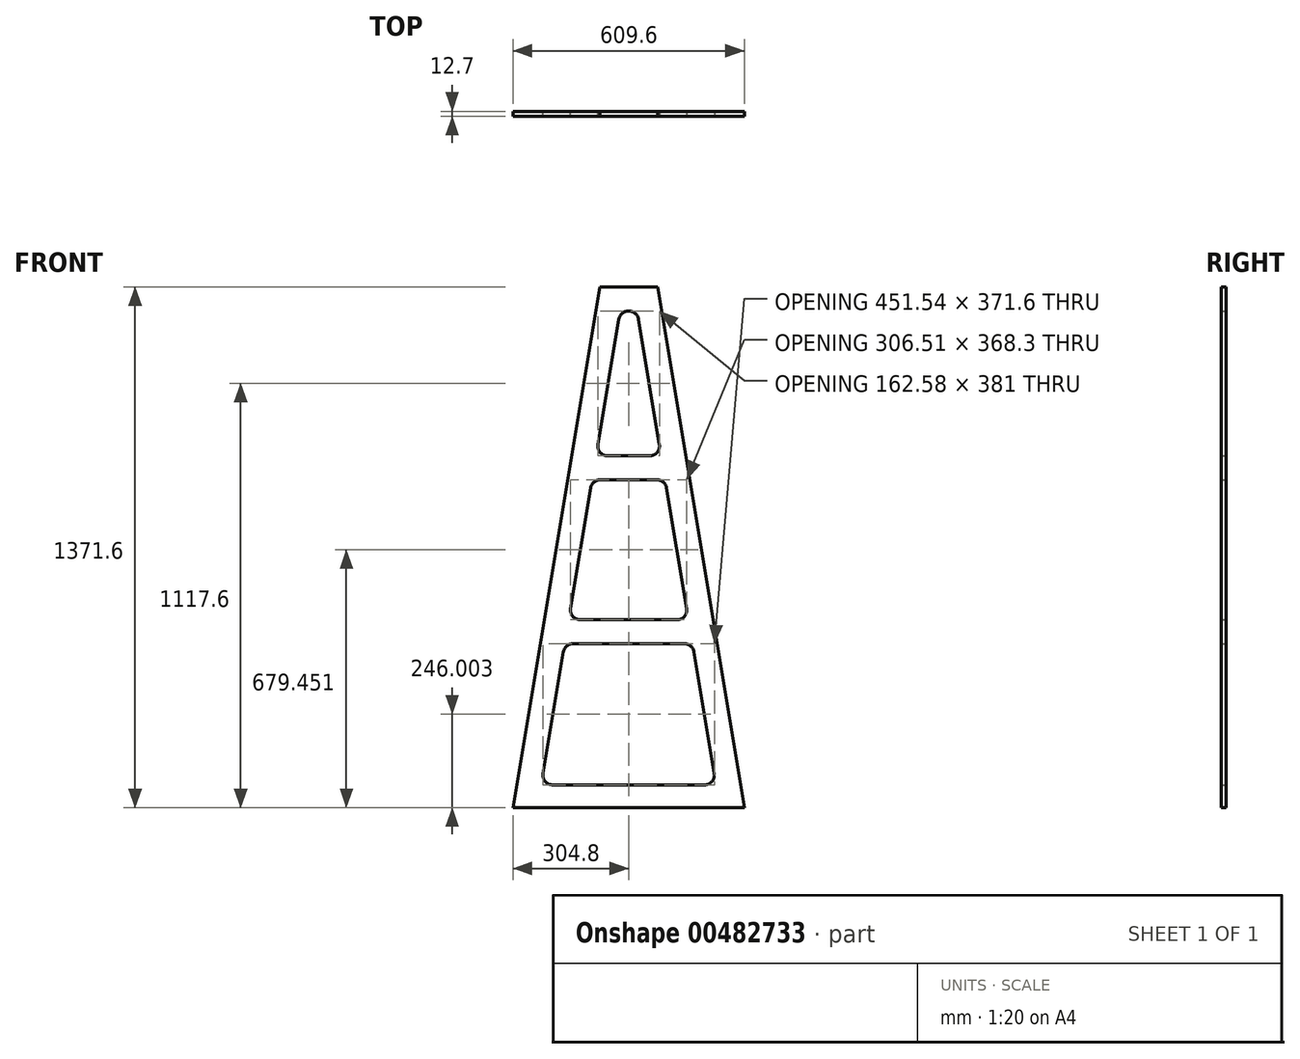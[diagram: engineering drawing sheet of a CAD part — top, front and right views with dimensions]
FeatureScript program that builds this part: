
annotation { "Feature Type Name" : "Feature", "Feature Type Description" : "" }
export const myFeature = defineFeature(function(context is Context, id is Id, definition is map)
    precondition{}
    {
        {
            var Q0;
            Q0=qCreatedBy(makeId("Front.planeOp"),FACE);
            var sketch = newSketch(context, id + "F0", { "sketchPlane" : qUnion([Q0])});
            skLineSegment(sketch, "E0", {"start": v(0, 220.15) * mm, "end": v(76.2, 220.15) * mm});
            skLineSegment(sketch, "E1", {"start": v(76.2, 220.15) * mm, "end": v(304.8, -1151.45) * mm});
            skLineSegment(sketch, "E2", {"start": v(304.8, -1151.45) * mm, "end": v(0, -1151.45) * mm});
            skLineSegment(sketch, "E3", {"start": v(0, -1151.45) * mm, "end": v(0, 220.15) * mm, "construction": true});
            skLineSegment(sketch, "E4", {"start": v(0, -1091.25) * mm, "end": v(230.4, -1091.25) * mm});
            skLineSegment(sketch, "E5", {"start": v(230.4, -1091.25) * mm, "end": v(168.46, -719.65) * mm});
            skLineSegment(sketch, "E6", {"start": v(168.46, -719.65) * mm, "end": v(0, -719.65) * mm});
            skLineSegment(sketch, "E7", {"start": v(0, -656.15) * mm, "end": v(157.87, -656.15) * mm});
            skLineSegment(sketch, "E8", {"start": v(157.87, -656.15) * mm, "end": v(96.5, -287.85) * mm});
            skLineSegment(sketch, "E9", {"start": v(96.5, -287.85) * mm, "end": v(0, -287.85) * mm});
            skLineSegment(sketch, "E10", {"start": v(0, -224.35) * mm, "end": v(85.9, -224.35) * mm});
            skLineSegment(sketch, "E11", {"start": v(85.9, -224.35) * mm, "end": v(22.4, 156.65) * mm});
            skLineSegment(sketch, "E12", {"start": v(22.4, 156.65) * mm, "end": v(0, 156.65) * mm});
            skLineSegment(sketch, "E13.MirrorCS", {"start": v(0, 220.15) * mm, "end": v(-76.2, 220.15) * mm});
            skLineSegment(sketch, "E14.MirrorCS", {"start": v(-76.2, 220.15) * mm, "end": v(-304.8, -1151.45) * mm});
            skLineSegment(sketch, "E15.MirrorCS", {"start": v(-304.8, -1151.45) * mm, "end": v(0, -1151.45) * mm});
            skLineSegment(sketch, "E16.MirrorCS", {"start": v(0, -1091.25) * mm, "end": v(-230.4, -1091.25) * mm});
            skLineSegment(sketch, "E17.MirrorCS", {"start": v(-230.4, -1091.25) * mm, "end": v(-168.46, -719.65) * mm});
            skLineSegment(sketch, "E18.MirrorCS", {"start": v(-168.46, -719.65) * mm, "end": v(0, -719.65) * mm});
            skLineSegment(sketch, "E19.MirrorCS", {"start": v(0, -656.15) * mm, "end": v(-157.87, -656.15) * mm});
            skLineSegment(sketch, "E20.MirrorCS", {"start": v(-96.5, -287.85) * mm, "end": v(0, -287.85) * mm});
            skLineSegment(sketch, "E21.MirrorCS", {"start": v(-157.87, -656.15) * mm, "end": v(-96.5, -287.85) * mm});
            skLineSegment(sketch, "E22.MirrorCS", {"start": v(0, -224.35) * mm, "end": v(-85.9, -224.35) * mm});
            skLineSegment(sketch, "E23.MirrorCS", {"start": v(-85.9, -224.35) * mm, "end": v(-22.4, 156.65) * mm});
            skLineSegment(sketch, "E24.MirrorCS", {"start": v(-22.4, 156.65) * mm, "end": v(0, 156.65) * mm});
            skSolve(sketch);
        }
        {
            var Q0;
            Q0=makeQuery(id+"F0.imprint","IMPRINT",FACE,{"disambiguationData":[TD([[makeQuery(id+"F0.imprint","IMPRINT",EDGE,{"derivedFrom":sQuery(id+"F0.wireOp",EDGE,"E0")}),-1.0]])]});
            extrude(context, id + "F1", {"entities" : qUnion([Q0]), "depth" : 12.7 * mm});
        }
        {
            var Q0;
            Q0=makeQuery(id+"F1.opExtrude","SWEPT_EDGE",EDGE,{"disambiguationData":[OSD([sQuery(id+"F0.wireOp",EDGE,"E22.MirrorCS"),sQuery(id+"F0.wireOp",EDGE,"E23.MirrorCS")])]});
            var Q1;
            Q1=makeQuery(id+"F1.opExtrude","SWEPT_EDGE",EDGE,{"disambiguationData":[OSD([sQuery(id+"F0.wireOp",EDGE,"E10"),sQuery(id+"F0.wireOp",EDGE,"E11")])]});
            var Q2;
            Q2=makeQuery(id+"F1.opExtrude","SWEPT_EDGE",EDGE,{"disambiguationData":[OSD([sQuery(id+"F0.wireOp",EDGE,"E11"),sQuery(id+"F0.wireOp",EDGE,"E12")])]});
            var Q3;
            Q3=makeQuery(id+"F1.opExtrude","SWEPT_EDGE",EDGE,{"disambiguationData":[OSD([sQuery(id+"F0.wireOp",EDGE,"E23.MirrorCS"),sQuery(id+"F0.wireOp",EDGE,"E24.MirrorCS")])]});
            var Q4;
            Q4=makeQuery(id+"F1.opExtrude","SWEPT_EDGE",EDGE,{"disambiguationData":[OSD([sQuery(id+"F0.wireOp",EDGE,"E20.MirrorCS"),sQuery(id+"F0.wireOp",EDGE,"E21.MirrorCS")])]});
            var Q5;
            Q5=makeQuery(id+"F1.opExtrude","SWEPT_EDGE",EDGE,{"disambiguationData":[OSD([sQuery(id+"F0.wireOp",EDGE,"E8"),sQuery(id+"F0.wireOp",EDGE,"E9")])]});
            var Q6;
            Q6=makeQuery(id+"F1.opExtrude","SWEPT_EDGE",EDGE,{"disambiguationData":[OSD([sQuery(id+"F0.wireOp",EDGE,"E7"),sQuery(id+"F0.wireOp",EDGE,"E8")])]});
            var Q7;
            Q7=makeQuery(id+"F1.opExtrude","SWEPT_EDGE",EDGE,{"disambiguationData":[OSD([sQuery(id+"F0.wireOp",EDGE,"E19.MirrorCS"),sQuery(id+"F0.wireOp",EDGE,"E21.MirrorCS")])]});
            var Q8;
            Q8=makeQuery(id+"F1.opExtrude","SWEPT_EDGE",EDGE,{"disambiguationData":[OSD([sQuery(id+"F0.wireOp",EDGE,"E16.MirrorCS"),sQuery(id+"F0.wireOp",EDGE,"E17.MirrorCS")])]});
            var Q9;
            Q9=makeQuery(id+"F1.opExtrude","SWEPT_EDGE",EDGE,{"disambiguationData":[OSD([sQuery(id+"F0.wireOp",EDGE,"E5"),sQuery(id+"F0.wireOp",EDGE,"E6")])]});
            var Q10;
            Q10=makeQuery(id+"F1.opExtrude","SWEPT_EDGE",EDGE,{"disambiguationData":[OSD([sQuery(id+"F0.wireOp",EDGE,"E4"),sQuery(id+"F0.wireOp",EDGE,"E5")])]});
            var Q11;
            Q11=makeQuery(id+"F1.opExtrude","SWEPT_EDGE",EDGE,{"disambiguationData":[OSD([sQuery(id+"F0.wireOp",EDGE,"E17.MirrorCS"),sQuery(id+"F0.wireOp",EDGE,"E18.MirrorCS")])]});
            fillet(context, id + "F2", {"entities" : qUnion([Q0, Q1, Q2, Q3, Q4, Q5, Q6, Q7, Q8, Q9, Q10, Q11]), "radius" : 25.4 * mm, "tangentPropagation" : true, "allowEdgeOverflow" : false});
        }
    });
